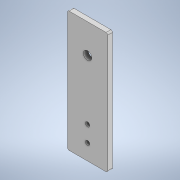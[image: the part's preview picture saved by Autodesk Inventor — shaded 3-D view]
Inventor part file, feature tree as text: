
AUTODESK INVENTOR PART (.ipt)
format: ipt  version: 2022 (Build 260153000, 153)  size: 117,760 bytes
history: native  units: mm
features: sketch x3, hole x2, extrude x1, fillet x1
ambient origin geometry x8: Origin, YZ Plane, XZ Plane, XY Plane, X Axis, Y Axis, Z Axis, Center Point
bodies: Solid1 (feature_tree)
feature tree (7):
  extrude  "Extrusion1"  Depth=150.0mm
  fillet  "Fillet1"  Radius=6.0mm
  hole  "Hole1"  [1 undecoded]
  hole  "Hole2"  [1 undecoded]
  sketch  "Sketch2"  dims[d0=50.0mm d1=150.0mm d2=6.0mm d3=0.0mm]
  sketch  "Sketch3"  dims[d4=2.0mm d5=36.4mm]
  sketch  "Sketch4"  dims[d6=10.5mm d7=6.0mm d8=4.0mm d9=2.0mm d10=90.0deg d11=8.0mm d12=20.594885mm d13=20.0mm d14=39.551mm d15=5.4mm d16=6.0mm d17=4.0mm d18=2.0mm d19=90.0deg d20=8.0mm d21=20.594885mm]
note: 2 required parameter values undecoded (feature->parameter linkage not recoverable at this tier; creation-order binding heuristic only, values carry confidence <= 0.55)
